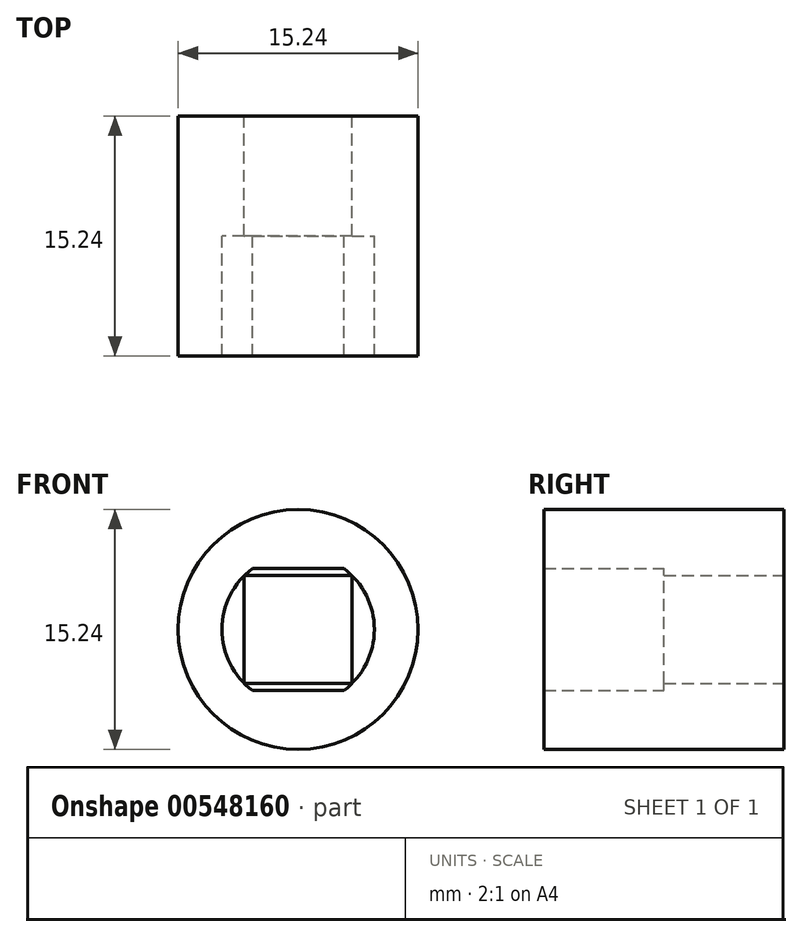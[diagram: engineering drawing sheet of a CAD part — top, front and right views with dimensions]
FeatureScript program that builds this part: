
annotation { "Feature Type Name" : "Feature", "Feature Type Description" : "" }
export const myFeature = defineFeature(function(context is Context, id is Id, definition is map)
    precondition{}
    {
        {
            var Q0;
            Q0=qCreatedBy(makeId("Front.planeOp"),FACE);
            var sketch = newSketch(context, id + "F0", { "sketchPlane" : qUnion([Q0])});
            skCircle(sketch, "E0", {"center": v(0, 0) * mm, "radius": 7.62 * mm});
            skLineSegment(sketch, "E1.bottom", {"start": v(3.43, -3.43) * mm, "end": v(-3.43, -3.43) * mm});
            skLineSegment(sketch, "E1.top", {"start": v(3.43, 3.43) * mm, "end": v(-3.43, 3.43) * mm});
            skLineSegment(sketch, "E1.left", {"start": v(3.43, -3.43) * mm, "end": v(3.43, 3.43) * mm});
            skLineSegment(sketch, "E1.right", {"start": v(-3.43, -3.43) * mm, "end": v(-3.43, 3.43) * mm});
            skSolve(sketch);
        }
        {
            var Q0;
            Q0 = qSketchRegion(id + "F0", true);
            extrude(context, id + "F1", {"entities" : qUnion([Q0]), "depth" : 7.62 * mm, "offsetDistance" : 25.4 * mm});
        }
        {
            var Q0;
            Q0=makeQuery(id+"F1.opExtrude","CAP_FACE",FACE,{"disambiguationData":[OSD([sQuery(id+"F0.wireOp",EDGE,"E0"),sQuery(id+"F0.wireOp",EDGE,"E1.bottom"),sQuery(id+"F0.wireOp",EDGE,"E1.top"),sQuery(id+"F0.wireOp",EDGE,"E1.left"),sQuery(id+"F0.wireOp",EDGE,"E1.right")])],"isStart":false});
            var sketch = newSketch(context, id + "F2", { "sketchPlane" : qUnion([Q0])});
            skCircle(sketch, "E2", {"center": v(0, 0) * mm, "radius": 7.62 * mm});
            skCircle(sketch, "E3", {"center": v(0, 0) * mm, "radius": 4.84 * mm});
            skLineSegment(sketch, "E4", {"start": v(-2.9, 3.87) * mm, "end": v(2.9, 3.87) * mm});
            skLineSegment(sketch, "E5", {"start": v(-2.9, -3.87) * mm, "end": v(2.9, -3.87) * mm});
            skSolve(sketch);
        }
        {
            var Q0;
            Q0 = qSketchRegion(id + "F2", true);
            var Q1;
            {var subQ0=sQuery(id+"F2.wireOp",EDGE,"E4");Q1=makeQuery(id+"F2.imprint","IMPRINT",FACE,{"disambiguationData":[TD([[makeQuery(id+"F2.imprint","IMPRINT",EDGE,{"derivedFrom":subQ0}),1.0]])]});}
            var Q2;
            {var subQ0=sQuery(id+"F2.wireOp",EDGE,"E5");Q2=makeQuery(id+"F2.imprint","IMPRINT",FACE,{"disambiguationData":[TD([[makeQuery(id+"F2.imprint","IMPRINT",EDGE,{"derivedFrom":subQ0}),-1.0]])]});}
            extrude(context, id + "F3", {"entities" : qUnion([Q0, Q1, Q2]), "operationType" : NewBodyOperationType.ADD, "depth" : 7.62 * mm, "offsetDistance" : 25.4 * mm});
        }
    });
